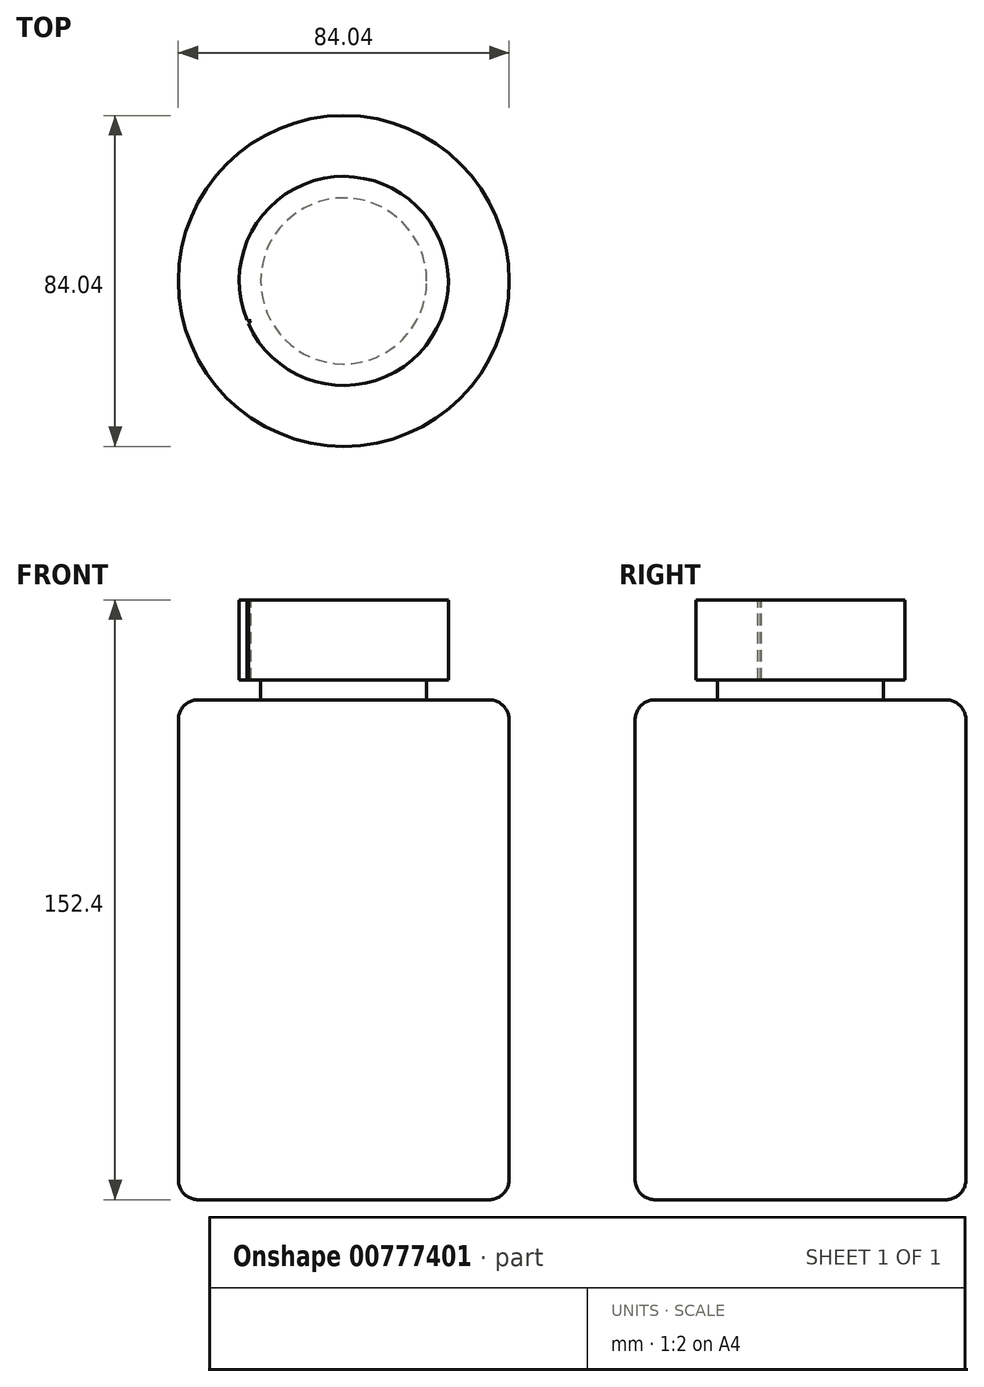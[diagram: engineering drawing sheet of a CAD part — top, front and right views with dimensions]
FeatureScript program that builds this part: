
annotation { "Feature Type Name" : "Feature", "Feature Type Description" : "" }
export const myFeature = defineFeature(function(context is Context, id is Id, definition is map)
    precondition{}
    {
        {
            var Q0;
            Q0=qCreatedBy(makeId("Top.planeOp"),FACE);
            var sketch = newSketch(context, id + "F0", { "sketchPlane" : qUnion([Q0])});
            skCircle(sketch, "E0", {"center": v(0, 0) * mm, "radius": 26.56 * mm});
            skSolve(sketch);
        }
        {
            var Q0;
            Q0 = qSketchRegion(id + "F0", true);
            extrude(context, id + "F1", {"entities" : qUnion([Q0]), "depth" : 20.32 * mm, "offsetDistance" : 25.4 * mm});
        }
        {
            var Q0;
            Q0=qCreatedBy(makeId("Top.planeOp"),FACE);
            var sketch = newSketch(context, id + "F2", { "sketchPlane" : qUnion([Q0])});
            skCircle(sketch, "E1", {"center": v(0, 0) * mm, "radius": 21.09 * mm});
            skSolve(sketch);
        }
        {
            var Q0;
            Q0 = qSketchRegion(id + "F2", true);
            extrude(context, id + "F3", {"entities" : qUnion([Q0]), "operationType" : NewBodyOperationType.ADD, "oppositeDirection" : true, "depth" : 5.08 * mm, "offsetDistance" : 25.4 * mm});
        }
        {
            var Q0;
            Q0=qCreatedBy(makeId("Top.planeOp"),FACE);
            cPlane(context, id + "F4", {"entities" : qUnion([Q0]), "cplaneType" : CPlaneType.OFFSET, "offset" : 5.08 * mm, "oppositeDirection" : true, "width" : 152.4 * mm, "height" : 152.4 * mm});
        }
        {
            var Q0;
            Q0=qCreatedBy(id+"F4.planeOp",FACE);
            var sketch = newSketch(context, id + "F5", { "sketchPlane" : qUnion([Q0])});
            skCircle(sketch, "E2", {"center": v(0, 0) * mm, "radius": 42.02 * mm});
            skSolve(sketch);
        }
        {
            var Q0;
            Q0 = qSketchRegion(id + "F5", true);
            extrude(context, id + "F6", {"entities" : qUnion([Q0]), "operationType" : NewBodyOperationType.ADD, "oppositeDirection" : true, "depth" : 127 * mm, "offsetDistance" : 25.4 * mm});
        }
        {
            var Q0;
            Q0=makeQuery(id+"F6.opExtrude","SWEPT_FACE",FACE,{"disambiguationData":[OSD([sQuery(id+"F5.wireOp",EDGE,"E2")])]});
            fillet(context, id + "F7", {"entities" : qUnion([Q0]), "radius" : 5.08 * mm, "tangentPropagation" : true, "allowEdgeOverflow" : false});
        }
        {
            var Q0;
            Q0=qCreatedBy(makeId("Top.planeOp"),FACE);
            var sketch = newSketch(context, id + "F8", { "sketchPlane" : qUnion([Q0])});
            skCircle(sketch, "E3.cCircle", {"center": v(-67.83, 42.56) * mm, "radius": 11.03 * mm, "construction": true});
            skLineSegment(sketch, "E3.0", {"start": v(-54.4, 44.96) * mm, "end": v(-61.4, 30.54) * mm});
            skLineSegment(sketch, "E3.1", {"start": v(-61.4, 30.54) * mm, "end": v(-77.28, 32.73) * mm});
            skLineSegment(sketch, "E3.2", {"start": v(-77.28, 32.73) * mm, "end": v(-80.1, 48.51) * mm});
            skLineSegment(sketch, "E3.3", {"start": v(-80.1, 48.51) * mm, "end": v(-65.96, 56.07) * mm});
            skLineSegment(sketch, "E3.4", {"start": v(-65.96, 56.07) * mm, "end": v(-54.4, 44.96) * mm});
            skPoint(sketch, "E3.0.midPoint", {"position": v(-57.9, 37.75) * mm});
            skCircle(sketch, "E4.cCircle", {"center": v(-67.83, 42.56) * mm, "radius": 14.44 * mm, "construction": true});
            skLineSegment(sketch, "E4.0", {"start": v(-53.4, 53.05) * mm, "end": v(-53.4, 32.07) * mm});
            skLineSegment(sketch, "E4.1", {"start": v(-53.4, 32.07) * mm, "end": v(-73.34, 25.59) * mm});
            skLineSegment(sketch, "E4.2", {"start": v(-73.34, 25.59) * mm, "end": v(-85.67, 42.56) * mm});
            skLineSegment(sketch, "E4.3", {"start": v(-85.67, 42.56) * mm, "end": v(-73.34, 59.53) * mm});
            skLineSegment(sketch, "E4.4", {"start": v(-73.34, 59.53) * mm, "end": v(-53.4, 53.05) * mm});
            skPoint(sketch, "E4.0.midPoint", {"position": v(-53.4, 42.56) * mm});
            skSolve(sketch);
        }
        {
            var Q0;
            Q0=makeQuery(id+"F8.imprint","IMPRINT",FACE,{"disambiguationData":[TD([[makeQuery(id+"F8.imprint","IMPRINT",EDGE,{"derivedFrom":sQuery(id+"F8.wireOp",EDGE,"E3.0")}),-1.0]])]});
            extrude(context, id + "F9", {"entities" : qUnion([Q0]), "depth" : 25.4 * mm, "offsetDistance" : 25.4 * mm});
        }
        {
            var Q0;
            Q0=qCreatedBy(makeId("Top.planeOp"),FACE);
            var sketch = newSketch(context, id + "F10", { "sketchPlane" : qUnion([Q0])});
            skLineSegment(sketch, "E5", {"start": v(-42.9, 41.98) * mm, "end": v(-26.68, 62.34) * mm});
            skSolve(sketch);
        }
        {
            var Q0;
            Q0=makeQuery(id+"F9.opExtrude","SWEPT_FACE",FACE,{"disambiguationData":[OSD([sQuery(id+"F8.wireOp",EDGE,"E3.3")])]});
            var Q1;
            Q1=sQuery(id+"F10.wireOp",EDGE,"E5");
            sweep(context, id + "F11", {"operationType" : NewBodyOperationType.ADD, "profiles" : qUnion([Q0]), "path" : qUnion([Q1])});
        }
        {
            var Q0;
            Q0=qCreatedBy(makeId("Top.planeOp"),FACE);
            cPlane(context, id + "F12", {"entities" : qUnion([Q0]), "cplaneType" : CPlaneType.OFFSET, "offset" : 20.32 * mm, "width" : 152.4 * mm, "height" : 152.4 * mm});
        }
        {
            var Q0;
            Q0=qCreatedBy(id+"F12.planeOp",FACE);
            var sketch = newSketch(context, id + "F13", { "sketchPlane" : qUnion([Q0])});
            skLineSegment(sketch, "E6", {"start": v(-24.24, -10.84) * mm, "end": v(-23.58, -10.13) * mm});
            skLineSegment(sketch, "E7", {"start": v(-23.58, -10.13) * mm, "end": v(-24.62, -9.96) * mm});
            skArc(sketch, "E8", {"start": v(-24.62, -9.96) * mm, "mid": v(-24.46, -10.41) * mm, "end": v(-24.24, -10.84) * mm});
            skSolve(sketch);
        }
        {
            var Q0;
            Q0=makeQuery(id+"F9.opExtrude","SWEPT_BODY",BODY,{"disambiguationData":[OSD([sQuery(id+"F8.wireOp",EDGE,"E3.0"),sQuery(id+"F8.wireOp",EDGE,"E3.1"),sQuery(id+"F8.wireOp",EDGE,"E3.2"),sQuery(id+"F8.wireOp",EDGE,"E3.3"),sQuery(id+"F8.wireOp",EDGE,"E3.4")])]});
            deleteBodies(context, id + "F14", {"entities" : qUnion([Q0])});
        }
        {
            var Q0;
            Q0=qCreatedBy(makeId("Front.planeOp"),FACE);
            var sketch = newSketch(context, id + "F15", { "sketchPlane" : qUnion([Q0])});
            skLineSegment(sketch, "E9", {"start": v(0, 34.42) * mm, "end": v(0, -30.59) * mm});
            skSolve(sketch);
        }
        {
            var Q0;
            Q0=makeQuery(id+"Fhpd5wwMVkgK8qK_1.97.F13.imprint","IMPRINT",FACE,{"disambiguationData":[TD([[makeQuery(id+"Fhpd5wwMVkgK8qK_1.97.F13.imprint","IMPRINT",EDGE,{"derivedFrom":sQuery(id+"Fhpd5wwMVkgK8qK_1.97.F13.wireOp",EDGE,"E6")}),1.0]])]});
            var Q1;
            Q1=makeQuery(id+"Fhpd5wwMVkgK8qK_1.4.F13.imprint","IMPRINT",FACE,{"disambiguationData":[TD([[makeQuery(id+"Fhpd5wwMVkgK8qK_1.4.F13.imprint","IMPRINT",EDGE,{"derivedFrom":sQuery(id+"Fhpd5wwMVkgK8qK_1.4.F13.wireOp",EDGE,"E6")}),1.0]])]});
            var Q2;
            Q2=makeQuery(id+"Fhpd5wwMVkgK8qK_1.50.F13.imprint","IMPRINT",FACE,{"disambiguationData":[TD([[makeQuery(id+"Fhpd5wwMVkgK8qK_1.50.F13.imprint","IMPRINT",EDGE,{"derivedFrom":sQuery(id+"Fhpd5wwMVkgK8qK_1.50.F13.wireOp",EDGE,"E6")}),1.0]])]});
            var Q3;
            Q3=makeQuery(id+"Fhpd5wwMVkgK8qK_1.19.F13.imprint","IMPRINT",FACE,{"disambiguationData":[TD([[makeQuery(id+"Fhpd5wwMVkgK8qK_1.19.F13.imprint","IMPRINT",EDGE,{"derivedFrom":sQuery(id+"Fhpd5wwMVkgK8qK_1.19.F13.wireOp",EDGE,"E6")}),1.0]])]});
            var Q4;
            Q4=makeQuery(id+"Fhpd5wwMVkgK8qK_1.14.F13.imprint","IMPRINT",FACE,{"disambiguationData":[TD([[makeQuery(id+"Fhpd5wwMVkgK8qK_1.14.F13.imprint","IMPRINT",EDGE,{"derivedFrom":sQuery(id+"Fhpd5wwMVkgK8qK_1.14.F13.wireOp",EDGE,"E6")}),1.0]])]});
            var Q5;
            Q5=makeQuery(id+"Fhpd5wwMVkgK8qK_1.15.F13.imprint","IMPRINT",FACE,{"disambiguationData":[TD([[makeQuery(id+"Fhpd5wwMVkgK8qK_1.15.F13.imprint","IMPRINT",EDGE,{"derivedFrom":sQuery(id+"Fhpd5wwMVkgK8qK_1.15.F13.wireOp",EDGE,"E6")}),1.0]])]});
            var Q6;
            Q6=makeQuery(id+"Fhpd5wwMVkgK8qK_1.90.F13.imprint","IMPRINT",FACE,{"disambiguationData":[TD([[makeQuery(id+"Fhpd5wwMVkgK8qK_1.90.F13.imprint","IMPRINT",EDGE,{"derivedFrom":sQuery(id+"Fhpd5wwMVkgK8qK_1.90.F13.wireOp",EDGE,"E6")}),1.0]])]});
            var Q7;
            Q7=makeQuery(id+"Fhpd5wwMVkgK8qK_1.88.F13.imprint","IMPRINT",FACE,{"disambiguationData":[TD([[makeQuery(id+"Fhpd5wwMVkgK8qK_1.88.F13.imprint","IMPRINT",EDGE,{"derivedFrom":sQuery(id+"Fhpd5wwMVkgK8qK_1.88.F13.wireOp",EDGE,"E6")}),1.0]])]});
            var Q8;
            Q8=makeQuery(id+"Fhpd5wwMVkgK8qK_1.20.F13.imprint","IMPRINT",FACE,{"disambiguationData":[TD([[makeQuery(id+"Fhpd5wwMVkgK8qK_1.20.F13.imprint","IMPRINT",EDGE,{"derivedFrom":sQuery(id+"Fhpd5wwMVkgK8qK_1.20.F13.wireOp",EDGE,"E6")}),1.0]])]});
            var Q9;
            Q9=makeQuery(id+"Fhpd5wwMVkgK8qK_1.18.F13.imprint","IMPRINT",FACE,{"disambiguationData":[TD([[makeQuery(id+"Fhpd5wwMVkgK8qK_1.18.F13.imprint","IMPRINT",EDGE,{"derivedFrom":sQuery(id+"Fhpd5wwMVkgK8qK_1.18.F13.wireOp",EDGE,"E6")}),1.0]])]});
            var Q10;
            Q10=makeQuery(id+"Fhpd5wwMVkgK8qK_1.13.F13.imprint","IMPRINT",FACE,{"disambiguationData":[TD([[makeQuery(id+"Fhpd5wwMVkgK8qK_1.13.F13.imprint","IMPRINT",EDGE,{"derivedFrom":sQuery(id+"Fhpd5wwMVkgK8qK_1.13.F13.wireOp",EDGE,"E6")}),1.0]])]});
            var Q11;
            Q11=makeQuery(id+"Fhpd5wwMVkgK8qK_1.48.F13.imprint","IMPRINT",FACE,{"disambiguationData":[TD([[makeQuery(id+"Fhpd5wwMVkgK8qK_1.48.F13.imprint","IMPRINT",EDGE,{"derivedFrom":sQuery(id+"Fhpd5wwMVkgK8qK_1.48.F13.wireOp",EDGE,"E6")}),1.0]])]});
            var Q12;
            Q12=makeQuery(id+"Fhpd5wwMVkgK8qK_1.5.F13.imprint","IMPRINT",FACE,{"disambiguationData":[TD([[makeQuery(id+"Fhpd5wwMVkgK8qK_1.5.F13.imprint","IMPRINT",EDGE,{"derivedFrom":sQuery(id+"Fhpd5wwMVkgK8qK_1.5.F13.wireOp",EDGE,"E6")}),1.0]])]});
            var Q13;
            Q13=makeQuery(id+"Fhpd5wwMVkgK8qK_1.96.F13.imprint","IMPRINT",FACE,{"disambiguationData":[TD([[makeQuery(id+"Fhpd5wwMVkgK8qK_1.96.F13.imprint","IMPRINT",EDGE,{"derivedFrom":sQuery(id+"Fhpd5wwMVkgK8qK_1.96.F13.wireOp",EDGE,"E6")}),1.0]])]});
            var Q14;
            Q14=makeQuery(id+"Fhpd5wwMVkgK8qK_1.69.F13.imprint","IMPRINT",FACE,{"disambiguationData":[TD([[makeQuery(id+"Fhpd5wwMVkgK8qK_1.69.F13.imprint","IMPRINT",EDGE,{"derivedFrom":sQuery(id+"Fhpd5wwMVkgK8qK_1.69.F13.wireOp",EDGE,"E6")}),1.0]])]});
            var Q15;
            Q15=makeQuery(id+"Fhpd5wwMVkgK8qK_1.45.F13.imprint","IMPRINT",FACE,{"disambiguationData":[TD([[makeQuery(id+"Fhpd5wwMVkgK8qK_1.45.F13.imprint","IMPRINT",EDGE,{"derivedFrom":sQuery(id+"Fhpd5wwMVkgK8qK_1.45.F13.wireOp",EDGE,"E6")}),1.0]])]});
            var Q16;
            Q16=makeQuery(id+"Fhpd5wwMVkgK8qK_1.68.F13.imprint","IMPRINT",FACE,{"disambiguationData":[TD([[makeQuery(id+"Fhpd5wwMVkgK8qK_1.68.F13.imprint","IMPRINT",EDGE,{"derivedFrom":sQuery(id+"Fhpd5wwMVkgK8qK_1.68.F13.wireOp",EDGE,"E6")}),1.0]])]});
            var Q17;
            Q17=makeQuery(id+"Fhpd5wwMVkgK8qK_1.1.F13.imprint","IMPRINT",FACE,{"disambiguationData":[TD([[makeQuery(id+"Fhpd5wwMVkgK8qK_1.1.F13.imprint","IMPRINT",EDGE,{"derivedFrom":sQuery(id+"Fhpd5wwMVkgK8qK_1.1.F13.wireOp",EDGE,"E6")}),1.0]])]});
            var Q18;
            Q18=makeQuery(id+"Fhpd5wwMVkgK8qK_1.8.F13.imprint","IMPRINT",FACE,{"disambiguationData":[TD([[makeQuery(id+"Fhpd5wwMVkgK8qK_1.8.F13.imprint","IMPRINT",EDGE,{"derivedFrom":sQuery(id+"Fhpd5wwMVkgK8qK_1.8.F13.wireOp",EDGE,"E6")}),1.0]])]});
            var Q19;
            Q19=makeQuery(id+"Fhpd5wwMVkgK8qK_1.9.F13.imprint","IMPRINT",FACE,{"disambiguationData":[TD([[makeQuery(id+"Fhpd5wwMVkgK8qK_1.9.F13.imprint","IMPRINT",EDGE,{"derivedFrom":sQuery(id+"Fhpd5wwMVkgK8qK_1.9.F13.wireOp",EDGE,"E6")}),1.0]])]});
            var Q20;
            Q20=makeQuery(id+"Fhpd5wwMVkgK8qK_1.37.F13.imprint","IMPRINT",FACE,{"disambiguationData":[TD([[makeQuery(id+"Fhpd5wwMVkgK8qK_1.37.F13.imprint","IMPRINT",EDGE,{"derivedFrom":sQuery(id+"Fhpd5wwMVkgK8qK_1.37.F13.wireOp",EDGE,"E6")}),1.0]])]});
            var Q21;
            Q21=makeQuery(id+"Fhpd5wwMVkgK8qK_1.21.F13.imprint","IMPRINT",FACE,{"disambiguationData":[TD([[makeQuery(id+"Fhpd5wwMVkgK8qK_1.21.F13.imprint","IMPRINT",EDGE,{"derivedFrom":sQuery(id+"Fhpd5wwMVkgK8qK_1.21.F13.wireOp",EDGE,"E6")}),1.0]])]});
            var Q22;
            Q22=makeQuery(id+"Fhpd5wwMVkgK8qK_1.99.F13.imprint","IMPRINT",FACE,{"disambiguationData":[TD([[makeQuery(id+"Fhpd5wwMVkgK8qK_1.99.F13.imprint","IMPRINT",EDGE,{"derivedFrom":sQuery(id+"Fhpd5wwMVkgK8qK_1.99.F13.wireOp",EDGE,"E6")}),1.0]])]});
            var Q23;
            Q23=makeQuery(id+"Fhpd5wwMVkgK8qK_1.17.F13.imprint","IMPRINT",FACE,{"disambiguationData":[TD([[makeQuery(id+"Fhpd5wwMVkgK8qK_1.17.F13.imprint","IMPRINT",EDGE,{"derivedFrom":sQuery(id+"Fhpd5wwMVkgK8qK_1.17.F13.wireOp",EDGE,"E6")}),1.0]])]});
            var Q24;
            Q24=makeQuery(id+"Fhpd5wwMVkgK8qK_1.38.F13.imprint","IMPRINT",FACE,{"disambiguationData":[TD([[makeQuery(id+"Fhpd5wwMVkgK8qK_1.38.F13.imprint","IMPRINT",EDGE,{"derivedFrom":sQuery(id+"Fhpd5wwMVkgK8qK_1.38.F13.wireOp",EDGE,"E6")}),1.0]])]});
            var Q25;
            Q25=makeQuery(id+"Fhpd5wwMVkgK8qK_1.66.F13.imprint","IMPRINT",FACE,{"disambiguationData":[TD([[makeQuery(id+"Fhpd5wwMVkgK8qK_1.66.F13.imprint","IMPRINT",EDGE,{"derivedFrom":sQuery(id+"Fhpd5wwMVkgK8qK_1.66.F13.wireOp",EDGE,"E6")}),1.0]])]});
            var Q26;
            Q26=makeQuery(id+"Fhpd5wwMVkgK8qK_1.34.F13.imprint","IMPRINT",FACE,{"disambiguationData":[TD([[makeQuery(id+"Fhpd5wwMVkgK8qK_1.34.F13.imprint","IMPRINT",EDGE,{"derivedFrom":sQuery(id+"Fhpd5wwMVkgK8qK_1.34.F13.wireOp",EDGE,"E6")}),1.0]])]});
            var Q27;
            Q27=makeQuery(id+"Fhpd5wwMVkgK8qK_1.52.F13.imprint","IMPRINT",FACE,{"disambiguationData":[TD([[makeQuery(id+"Fhpd5wwMVkgK8qK_1.52.F13.imprint","IMPRINT",EDGE,{"derivedFrom":sQuery(id+"Fhpd5wwMVkgK8qK_1.52.F13.wireOp",EDGE,"E6")}),1.0]])]});
            var Q28;
            Q28=makeQuery(id+"F13.imprint","IMPRINT",FACE,{"disambiguationData":[TD([[makeQuery(id+"F13.imprint","IMPRINT",EDGE,{"derivedFrom":sQuery(id+"F13.wireOp",EDGE,"E6")}),1.0]])]});
            var Q29;
            Q29=makeQuery(id+"Fhpd5wwMVkgK8qK_1.22.F13.imprint","IMPRINT",FACE,{"disambiguationData":[TD([[makeQuery(id+"Fhpd5wwMVkgK8qK_1.22.F13.imprint","IMPRINT",EDGE,{"derivedFrom":sQuery(id+"Fhpd5wwMVkgK8qK_1.22.F13.wireOp",EDGE,"E6")}),1.0]])]});
            var Q30;
            Q30=makeQuery(id+"Fhpd5wwMVkgK8qK_1.44.F13.imprint","IMPRINT",FACE,{"disambiguationData":[TD([[makeQuery(id+"Fhpd5wwMVkgK8qK_1.44.F13.imprint","IMPRINT",EDGE,{"derivedFrom":sQuery(id+"Fhpd5wwMVkgK8qK_1.44.F13.wireOp",EDGE,"E6")}),1.0]])]});
            var Q31;
            Q31=makeQuery(id+"Fhpd5wwMVkgK8qK_1.6.F13.imprint","IMPRINT",FACE,{"disambiguationData":[TD([[makeQuery(id+"Fhpd5wwMVkgK8qK_1.6.F13.imprint","IMPRINT",EDGE,{"derivedFrom":sQuery(id+"Fhpd5wwMVkgK8qK_1.6.F13.wireOp",EDGE,"E6")}),1.0]])]});
            var Q32;
            Q32=makeQuery(id+"Fhpd5wwMVkgK8qK_1.98.F13.imprint","IMPRINT",FACE,{"disambiguationData":[TD([[makeQuery(id+"Fhpd5wwMVkgK8qK_1.98.F13.imprint","IMPRINT",EDGE,{"derivedFrom":sQuery(id+"Fhpd5wwMVkgK8qK_1.98.F13.wireOp",EDGE,"E6")}),1.0]])]});
            var Q33;
            Q33=makeQuery(id+"Fhpd5wwMVkgK8qK_1.11.F13.imprint","IMPRINT",FACE,{"disambiguationData":[TD([[makeQuery(id+"Fhpd5wwMVkgK8qK_1.11.F13.imprint","IMPRINT",EDGE,{"derivedFrom":sQuery(id+"Fhpd5wwMVkgK8qK_1.11.F13.wireOp",EDGE,"E6")}),1.0]])]});
            var Q34;
            Q34=makeQuery(id+"Fhpd5wwMVkgK8qK_1.10.F13.imprint","IMPRINT",FACE,{"disambiguationData":[TD([[makeQuery(id+"Fhpd5wwMVkgK8qK_1.10.F13.imprint","IMPRINT",EDGE,{"derivedFrom":sQuery(id+"Fhpd5wwMVkgK8qK_1.10.F13.wireOp",EDGE,"E6")}),1.0]])]});
            var Q35;
            Q35=makeQuery(id+"Fhpd5wwMVkgK8qK_1.7.F13.imprint","IMPRINT",FACE,{"disambiguationData":[TD([[makeQuery(id+"Fhpd5wwMVkgK8qK_1.7.F13.imprint","IMPRINT",EDGE,{"derivedFrom":sQuery(id+"Fhpd5wwMVkgK8qK_1.7.F13.wireOp",EDGE,"E6")}),1.0]])]});
            var Q36;
            Q36=makeQuery(id+"Fhpd5wwMVkgK8qK_1.75.F13.imprint","IMPRINT",FACE,{"disambiguationData":[TD([[makeQuery(id+"Fhpd5wwMVkgK8qK_1.75.F13.imprint","IMPRINT",EDGE,{"derivedFrom":sQuery(id+"Fhpd5wwMVkgK8qK_1.75.F13.wireOp",EDGE,"E6")}),1.0]])]});
            var Q37;
            Q37=makeQuery(id+"Fhpd5wwMVkgK8qK_1.65.F13.imprint","IMPRINT",FACE,{"disambiguationData":[TD([[makeQuery(id+"Fhpd5wwMVkgK8qK_1.65.F13.imprint","IMPRINT",EDGE,{"derivedFrom":sQuery(id+"Fhpd5wwMVkgK8qK_1.65.F13.wireOp",EDGE,"E6")}),1.0]])]});
            var Q38;
            Q38=makeQuery(id+"Fhpd5wwMVkgK8qK_1.89.F13.imprint","IMPRINT",FACE,{"disambiguationData":[TD([[makeQuery(id+"Fhpd5wwMVkgK8qK_1.89.F13.imprint","IMPRINT",EDGE,{"derivedFrom":sQuery(id+"Fhpd5wwMVkgK8qK_1.89.F13.wireOp",EDGE,"E6")}),1.0]])]});
            var Q39;
            Q39=makeQuery(id+"Fhpd5wwMVkgK8qK_1.91.F13.imprint","IMPRINT",FACE,{"disambiguationData":[TD([[makeQuery(id+"Fhpd5wwMVkgK8qK_1.91.F13.imprint","IMPRINT",EDGE,{"derivedFrom":sQuery(id+"Fhpd5wwMVkgK8qK_1.91.F13.wireOp",EDGE,"E6")}),1.0]])]});
            var Q40;
            Q40=makeQuery(id+"Fhpd5wwMVkgK8qK_1.71.F13.imprint","IMPRINT",FACE,{"disambiguationData":[TD([[makeQuery(id+"Fhpd5wwMVkgK8qK_1.71.F13.imprint","IMPRINT",EDGE,{"derivedFrom":sQuery(id+"Fhpd5wwMVkgK8qK_1.71.F13.wireOp",EDGE,"E6")}),1.0]])]});
            var Q41;
            Q41=makeQuery(id+"Fhpd5wwMVkgK8qK_1.16.F13.imprint","IMPRINT",FACE,{"disambiguationData":[TD([[makeQuery(id+"Fhpd5wwMVkgK8qK_1.16.F13.imprint","IMPRINT",EDGE,{"derivedFrom":sQuery(id+"Fhpd5wwMVkgK8qK_1.16.F13.wireOp",EDGE,"E6")}),1.0]])]});
            var Q42;
            Q42=makeQuery(id+"Fhpd5wwMVkgK8qK_1.92.F13.imprint","IMPRINT",FACE,{"disambiguationData":[TD([[makeQuery(id+"Fhpd5wwMVkgK8qK_1.92.F13.imprint","IMPRINT",EDGE,{"derivedFrom":sQuery(id+"Fhpd5wwMVkgK8qK_1.92.F13.wireOp",EDGE,"E6")}),1.0]])]});
            var Q43;
            Q43=makeQuery(id+"Fhpd5wwMVkgK8qK_1.49.F13.imprint","IMPRINT",FACE,{"disambiguationData":[TD([[makeQuery(id+"Fhpd5wwMVkgK8qK_1.49.F13.imprint","IMPRINT",EDGE,{"derivedFrom":sQuery(id+"Fhpd5wwMVkgK8qK_1.49.F13.wireOp",EDGE,"E6")}),1.0]])]});
            var Q44;
            Q44=makeQuery(id+"Fhpd5wwMVkgK8qK_1.46.F13.imprint","IMPRINT",FACE,{"disambiguationData":[TD([[makeQuery(id+"Fhpd5wwMVkgK8qK_1.46.F13.imprint","IMPRINT",EDGE,{"derivedFrom":sQuery(id+"Fhpd5wwMVkgK8qK_1.46.F13.wireOp",EDGE,"E6")}),1.0]])]});
            var Q45;
            Q45=makeQuery(id+"Fhpd5wwMVkgK8qK_1.2.F13.imprint","IMPRINT",FACE,{"disambiguationData":[TD([[makeQuery(id+"Fhpd5wwMVkgK8qK_1.2.F13.imprint","IMPRINT",EDGE,{"derivedFrom":sQuery(id+"Fhpd5wwMVkgK8qK_1.2.F13.wireOp",EDGE,"E6")}),1.0]])]});
            var Q46;
            Q46=makeQuery(id+"Fhpd5wwMVkgK8qK_1.3.F13.imprint","IMPRINT",FACE,{"disambiguationData":[TD([[makeQuery(id+"Fhpd5wwMVkgK8qK_1.3.F13.imprint","IMPRINT",EDGE,{"derivedFrom":sQuery(id+"Fhpd5wwMVkgK8qK_1.3.F13.wireOp",EDGE,"E6")}),1.0]])]});
            var Q47;
            Q47=makeQuery(id+"Fhpd5wwMVkgK8qK_1.93.F13.imprint","IMPRINT",FACE,{"disambiguationData":[TD([[makeQuery(id+"Fhpd5wwMVkgK8qK_1.93.F13.imprint","IMPRINT",EDGE,{"derivedFrom":sQuery(id+"Fhpd5wwMVkgK8qK_1.93.F13.wireOp",EDGE,"E6")}),1.0]])]});
            var Q48;
            Q48=makeQuery(id+"Fhpd5wwMVkgK8qK_1.23.F13.imprint","IMPRINT",FACE,{"disambiguationData":[TD([[makeQuery(id+"Fhpd5wwMVkgK8qK_1.23.F13.imprint","IMPRINT",EDGE,{"derivedFrom":sQuery(id+"Fhpd5wwMVkgK8qK_1.23.F13.wireOp",EDGE,"E6")}),1.0]])]});
            var Q49;
            Q49=makeQuery(id+"Fhpd5wwMVkgK8qK_1.87.F13.imprint","IMPRINT",FACE,{"disambiguationData":[TD([[makeQuery(id+"Fhpd5wwMVkgK8qK_1.87.F13.imprint","IMPRINT",EDGE,{"derivedFrom":sQuery(id+"Fhpd5wwMVkgK8qK_1.87.F13.wireOp",EDGE,"E6")}),1.0]])]});
            var Q50;
            Q50=makeQuery(id+"Fhpd5wwMVkgK8qK_1.67.F13.imprint","IMPRINT",FACE,{"disambiguationData":[TD([[makeQuery(id+"Fhpd5wwMVkgK8qK_1.67.F13.imprint","IMPRINT",EDGE,{"derivedFrom":sQuery(id+"Fhpd5wwMVkgK8qK_1.67.F13.wireOp",EDGE,"E6")}),1.0]])]});
            var Q51;
            Q51=makeQuery(id+"Fhpd5wwMVkgK8qK_1.47.F13.imprint","IMPRINT",FACE,{"disambiguationData":[TD([[makeQuery(id+"Fhpd5wwMVkgK8qK_1.47.F13.imprint","IMPRINT",EDGE,{"derivedFrom":sQuery(id+"Fhpd5wwMVkgK8qK_1.47.F13.wireOp",EDGE,"E6")}),1.0]])]});
            var Q52;
            Q52=makeQuery(id+"Fhpd5wwMVkgK8qK_1.85.F13.imprint","IMPRINT",FACE,{"disambiguationData":[TD([[makeQuery(id+"Fhpd5wwMVkgK8qK_1.85.F13.imprint","IMPRINT",EDGE,{"derivedFrom":sQuery(id+"Fhpd5wwMVkgK8qK_1.85.F13.wireOp",EDGE,"E6")}),1.0]])]});
            var Q53;
            Q53=makeQuery(id+"Fhpd5wwMVkgK8qK_1.53.F13.imprint","IMPRINT",FACE,{"disambiguationData":[TD([[makeQuery(id+"Fhpd5wwMVkgK8qK_1.53.F13.imprint","IMPRINT",EDGE,{"derivedFrom":sQuery(id+"Fhpd5wwMVkgK8qK_1.53.F13.wireOp",EDGE,"E6")}),1.0]])]});
            var Q54;
            Q54=makeQuery(id+"Fhpd5wwMVkgK8qK_1.33.F13.imprint","IMPRINT",FACE,{"disambiguationData":[TD([[makeQuery(id+"Fhpd5wwMVkgK8qK_1.33.F13.imprint","IMPRINT",EDGE,{"derivedFrom":sQuery(id+"Fhpd5wwMVkgK8qK_1.33.F13.wireOp",EDGE,"E6")}),1.0]])]});
            var Q55;
            Q55=makeQuery(id+"Fhpd5wwMVkgK8qK_1.95.F13.imprint","IMPRINT",FACE,{"disambiguationData":[TD([[makeQuery(id+"Fhpd5wwMVkgK8qK_1.95.F13.imprint","IMPRINT",EDGE,{"derivedFrom":sQuery(id+"Fhpd5wwMVkgK8qK_1.95.F13.wireOp",EDGE,"E6")}),1.0]])]});
            var Q56;
            Q56=makeQuery(id+"Fhpd5wwMVkgK8qK_1.12.F13.imprint","IMPRINT",FACE,{"disambiguationData":[TD([[makeQuery(id+"Fhpd5wwMVkgK8qK_1.12.F13.imprint","IMPRINT",EDGE,{"derivedFrom":sQuery(id+"Fhpd5wwMVkgK8qK_1.12.F13.wireOp",EDGE,"E6")}),1.0]])]});
            var Q57;
            Q57=makeQuery(id+"Fhpd5wwMVkgK8qK_1.94.F13.imprint","IMPRINT",FACE,{"disambiguationData":[TD([[makeQuery(id+"Fhpd5wwMVkgK8qK_1.94.F13.imprint","IMPRINT",EDGE,{"derivedFrom":sQuery(id+"Fhpd5wwMVkgK8qK_1.94.F13.wireOp",EDGE,"E6")}),1.0]])]});
            var Q58;
            Q58=makeQuery(id+"Fhpd5wwMVkgK8qK_1.58.F13.imprint","IMPRINT",FACE,{"disambiguationData":[TD([[makeQuery(id+"Fhpd5wwMVkgK8qK_1.58.F13.imprint","IMPRINT",EDGE,{"derivedFrom":sQuery(id+"Fhpd5wwMVkgK8qK_1.58.F13.wireOp",EDGE,"E6")}),1.0]])]});
            var Q59;
            Q59=makeQuery(id+"Fhpd5wwMVkgK8qK_1.54.F13.imprint","IMPRINT",FACE,{"disambiguationData":[TD([[makeQuery(id+"Fhpd5wwMVkgK8qK_1.54.F13.imprint","IMPRINT",EDGE,{"derivedFrom":sQuery(id+"Fhpd5wwMVkgK8qK_1.54.F13.wireOp",EDGE,"E6")}),1.0]])]});
            var Q60;
            Q60=makeQuery(id+"Fhpd5wwMVkgK8qK_1.86.F13.imprint","IMPRINT",FACE,{"disambiguationData":[TD([[makeQuery(id+"Fhpd5wwMVkgK8qK_1.86.F13.imprint","IMPRINT",EDGE,{"derivedFrom":sQuery(id+"Fhpd5wwMVkgK8qK_1.86.F13.wireOp",EDGE,"E6")}),1.0]])]});
            var Q61;
            Q61=makeQuery(id+"Fhpd5wwMVkgK8qK_1.43.F13.imprint","IMPRINT",FACE,{"disambiguationData":[TD([[makeQuery(id+"Fhpd5wwMVkgK8qK_1.43.F13.imprint","IMPRINT",EDGE,{"derivedFrom":sQuery(id+"Fhpd5wwMVkgK8qK_1.43.F13.wireOp",EDGE,"E6")}),1.0]])]});
            var Q62;
            Q62=makeQuery(id+"Fhpd5wwMVkgK8qK_1.59.F13.imprint","IMPRINT",FACE,{"disambiguationData":[TD([[makeQuery(id+"Fhpd5wwMVkgK8qK_1.59.F13.imprint","IMPRINT",EDGE,{"derivedFrom":sQuery(id+"Fhpd5wwMVkgK8qK_1.59.F13.wireOp",EDGE,"E6")}),1.0]])]});
            var Q63;
            Q63=makeQuery(id+"Fhpd5wwMVkgK8qK_1.25.F13.imprint","IMPRINT",FACE,{"disambiguationData":[TD([[makeQuery(id+"Fhpd5wwMVkgK8qK_1.25.F13.imprint","IMPRINT",EDGE,{"derivedFrom":sQuery(id+"Fhpd5wwMVkgK8qK_1.25.F13.wireOp",EDGE,"E6")}),1.0]])]});
            var Q64;
            Q64=makeQuery(id+"Fhpd5wwMVkgK8qK_1.61.F13.imprint","IMPRINT",FACE,{"disambiguationData":[TD([[makeQuery(id+"Fhpd5wwMVkgK8qK_1.61.F13.imprint","IMPRINT",EDGE,{"derivedFrom":sQuery(id+"Fhpd5wwMVkgK8qK_1.61.F13.wireOp",EDGE,"E6")}),1.0]])]});
            var Q65;
            Q65=makeQuery(id+"Fhpd5wwMVkgK8qK_1.57.F13.imprint","IMPRINT",FACE,{"disambiguationData":[TD([[makeQuery(id+"Fhpd5wwMVkgK8qK_1.57.F13.imprint","IMPRINT",EDGE,{"derivedFrom":sQuery(id+"Fhpd5wwMVkgK8qK_1.57.F13.wireOp",EDGE,"E6")}),1.0]])]});
            var Q66;
            Q66=makeQuery(id+"Fhpd5wwMVkgK8qK_1.39.F13.imprint","IMPRINT",FACE,{"disambiguationData":[TD([[makeQuery(id+"Fhpd5wwMVkgK8qK_1.39.F13.imprint","IMPRINT",EDGE,{"derivedFrom":sQuery(id+"Fhpd5wwMVkgK8qK_1.39.F13.wireOp",EDGE,"E6")}),1.0]])]});
            var Q67;
            Q67=makeQuery(id+"Fhpd5wwMVkgK8qK_1.51.F13.imprint","IMPRINT",FACE,{"disambiguationData":[TD([[makeQuery(id+"Fhpd5wwMVkgK8qK_1.51.F13.imprint","IMPRINT",EDGE,{"derivedFrom":sQuery(id+"Fhpd5wwMVkgK8qK_1.51.F13.wireOp",EDGE,"E6")}),1.0]])]});
            var Q68;
            Q68=makeQuery(id+"Fhpd5wwMVkgK8qK_1.77.F13.imprint","IMPRINT",FACE,{"disambiguationData":[TD([[makeQuery(id+"Fhpd5wwMVkgK8qK_1.77.F13.imprint","IMPRINT",EDGE,{"derivedFrom":sQuery(id+"Fhpd5wwMVkgK8qK_1.77.F13.wireOp",EDGE,"E6")}),1.0]])]});
            var Q69;
            Q69=makeQuery(id+"Fhpd5wwMVkgK8qK_1.30.F13.imprint","IMPRINT",FACE,{"disambiguationData":[TD([[makeQuery(id+"Fhpd5wwMVkgK8qK_1.30.F13.imprint","IMPRINT",EDGE,{"derivedFrom":sQuery(id+"Fhpd5wwMVkgK8qK_1.30.F13.wireOp",EDGE,"E6")}),1.0]])]});
            var Q70;
            Q70=makeQuery(id+"Fhpd5wwMVkgK8qK_1.72.F13.imprint","IMPRINT",FACE,{"disambiguationData":[TD([[makeQuery(id+"Fhpd5wwMVkgK8qK_1.72.F13.imprint","IMPRINT",EDGE,{"derivedFrom":sQuery(id+"Fhpd5wwMVkgK8qK_1.72.F13.wireOp",EDGE,"E6")}),1.0]])]});
            var Q71;
            Q71=makeQuery(id+"Fhpd5wwMVkgK8qK_1.56.F13.imprint","IMPRINT",FACE,{"disambiguationData":[TD([[makeQuery(id+"Fhpd5wwMVkgK8qK_1.56.F13.imprint","IMPRINT",EDGE,{"derivedFrom":sQuery(id+"Fhpd5wwMVkgK8qK_1.56.F13.wireOp",EDGE,"E6")}),1.0]])]});
            var Q72;
            Q72=makeQuery(id+"Fhpd5wwMVkgK8qK_1.36.F13.imprint","IMPRINT",FACE,{"disambiguationData":[TD([[makeQuery(id+"Fhpd5wwMVkgK8qK_1.36.F13.imprint","IMPRINT",EDGE,{"derivedFrom":sQuery(id+"Fhpd5wwMVkgK8qK_1.36.F13.wireOp",EDGE,"E6")}),1.0]])]});
            var Q73;
            Q73=makeQuery(id+"Fhpd5wwMVkgK8qK_1.84.F13.imprint","IMPRINT",FACE,{"disambiguationData":[TD([[makeQuery(id+"Fhpd5wwMVkgK8qK_1.84.F13.imprint","IMPRINT",EDGE,{"derivedFrom":sQuery(id+"Fhpd5wwMVkgK8qK_1.84.F13.wireOp",EDGE,"E6")}),1.0]])]});
            var Q74;
            Q74=makeQuery(id+"Fhpd5wwMVkgK8qK_1.78.F13.imprint","IMPRINT",FACE,{"disambiguationData":[TD([[makeQuery(id+"Fhpd5wwMVkgK8qK_1.78.F13.imprint","IMPRINT",EDGE,{"derivedFrom":sQuery(id+"Fhpd5wwMVkgK8qK_1.78.F13.wireOp",EDGE,"E6")}),1.0]])]});
            var Q75;
            Q75=makeQuery(id+"Fhpd5wwMVkgK8qK_1.29.F13.imprint","IMPRINT",FACE,{"disambiguationData":[TD([[makeQuery(id+"Fhpd5wwMVkgK8qK_1.29.F13.imprint","IMPRINT",EDGE,{"derivedFrom":sQuery(id+"Fhpd5wwMVkgK8qK_1.29.F13.wireOp",EDGE,"E6")}),1.0]])]});
            var Q76;
            Q76=makeQuery(id+"Fhpd5wwMVkgK8qK_1.41.F13.imprint","IMPRINT",FACE,{"disambiguationData":[TD([[makeQuery(id+"Fhpd5wwMVkgK8qK_1.41.F13.imprint","IMPRINT",EDGE,{"derivedFrom":sQuery(id+"Fhpd5wwMVkgK8qK_1.41.F13.wireOp",EDGE,"E6")}),1.0]])]});
            var Q77;
            Q77=makeQuery(id+"Fhpd5wwMVkgK8qK_1.73.F13.imprint","IMPRINT",FACE,{"disambiguationData":[TD([[makeQuery(id+"Fhpd5wwMVkgK8qK_1.73.F13.imprint","IMPRINT",EDGE,{"derivedFrom":sQuery(id+"Fhpd5wwMVkgK8qK_1.73.F13.wireOp",EDGE,"E6")}),1.0]])]});
            var Q78;
            Q78=makeQuery(id+"Fhpd5wwMVkgK8qK_1.27.F13.imprint","IMPRINT",FACE,{"disambiguationData":[TD([[makeQuery(id+"Fhpd5wwMVkgK8qK_1.27.F13.imprint","IMPRINT",EDGE,{"derivedFrom":sQuery(id+"Fhpd5wwMVkgK8qK_1.27.F13.wireOp",EDGE,"E6")}),1.0]])]});
            var Q79;
            Q79=makeQuery(id+"Fhpd5wwMVkgK8qK_1.35.F13.imprint","IMPRINT",FACE,{"disambiguationData":[TD([[makeQuery(id+"Fhpd5wwMVkgK8qK_1.35.F13.imprint","IMPRINT",EDGE,{"derivedFrom":sQuery(id+"Fhpd5wwMVkgK8qK_1.35.F13.wireOp",EDGE,"E6")}),1.0]])]});
            var Q80;
            Q80=makeQuery(id+"Fhpd5wwMVkgK8qK_1.42.F13.imprint","IMPRINT",FACE,{"disambiguationData":[TD([[makeQuery(id+"Fhpd5wwMVkgK8qK_1.42.F13.imprint","IMPRINT",EDGE,{"derivedFrom":sQuery(id+"Fhpd5wwMVkgK8qK_1.42.F13.wireOp",EDGE,"E6")}),1.0]])]});
            var Q81;
            Q81=makeQuery(id+"Fhpd5wwMVkgK8qK_1.74.F13.imprint","IMPRINT",FACE,{"disambiguationData":[TD([[makeQuery(id+"Fhpd5wwMVkgK8qK_1.74.F13.imprint","IMPRINT",EDGE,{"derivedFrom":sQuery(id+"Fhpd5wwMVkgK8qK_1.74.F13.wireOp",EDGE,"E6")}),1.0]])]});
            var Q82;
            Q82=makeQuery(id+"Fhpd5wwMVkgK8qK_1.60.F13.imprint","IMPRINT",FACE,{"disambiguationData":[TD([[makeQuery(id+"Fhpd5wwMVkgK8qK_1.60.F13.imprint","IMPRINT",EDGE,{"derivedFrom":sQuery(id+"Fhpd5wwMVkgK8qK_1.60.F13.wireOp",EDGE,"E6")}),1.0]])]});
            var Q83;
            Q83=makeQuery(id+"Fhpd5wwMVkgK8qK_1.28.F13.imprint","IMPRINT",FACE,{"disambiguationData":[TD([[makeQuery(id+"Fhpd5wwMVkgK8qK_1.28.F13.imprint","IMPRINT",EDGE,{"derivedFrom":sQuery(id+"Fhpd5wwMVkgK8qK_1.28.F13.wireOp",EDGE,"E6")}),1.0]])]});
            var Q84;
            Q84=makeQuery(id+"Fhpd5wwMVkgK8qK_1.26.F13.imprint","IMPRINT",FACE,{"disambiguationData":[TD([[makeQuery(id+"Fhpd5wwMVkgK8qK_1.26.F13.imprint","IMPRINT",EDGE,{"derivedFrom":sQuery(id+"Fhpd5wwMVkgK8qK_1.26.F13.wireOp",EDGE,"E6")}),1.0]])]});
            var Q85;
            Q85=makeQuery(id+"Fhpd5wwMVkgK8qK_1.70.F13.imprint","IMPRINT",FACE,{"disambiguationData":[TD([[makeQuery(id+"Fhpd5wwMVkgK8qK_1.70.F13.imprint","IMPRINT",EDGE,{"derivedFrom":sQuery(id+"Fhpd5wwMVkgK8qK_1.70.F13.wireOp",EDGE,"E6")}),1.0]])]});
            var Q86;
            Q86=makeQuery(id+"Fhpd5wwMVkgK8qK_1.24.F13.imprint","IMPRINT",FACE,{"disambiguationData":[TD([[makeQuery(id+"Fhpd5wwMVkgK8qK_1.24.F13.imprint","IMPRINT",EDGE,{"derivedFrom":sQuery(id+"Fhpd5wwMVkgK8qK_1.24.F13.wireOp",EDGE,"E6")}),1.0]])]});
            var Q87;
            Q87=makeQuery(id+"Fhpd5wwMVkgK8qK_1.80.F13.imprint","IMPRINT",FACE,{"disambiguationData":[TD([[makeQuery(id+"Fhpd5wwMVkgK8qK_1.80.F13.imprint","IMPRINT",EDGE,{"derivedFrom":sQuery(id+"Fhpd5wwMVkgK8qK_1.80.F13.wireOp",EDGE,"E6")}),1.0]])]});
            var Q88;
            Q88=makeQuery(id+"Fhpd5wwMVkgK8qK_1.76.F13.imprint","IMPRINT",FACE,{"disambiguationData":[TD([[makeQuery(id+"Fhpd5wwMVkgK8qK_1.76.F13.imprint","IMPRINT",EDGE,{"derivedFrom":sQuery(id+"Fhpd5wwMVkgK8qK_1.76.F13.wireOp",EDGE,"E6")}),1.0]])]});
            var Q89;
            Q89=makeQuery(id+"Fhpd5wwMVkgK8qK_1.79.F13.imprint","IMPRINT",FACE,{"disambiguationData":[TD([[makeQuery(id+"Fhpd5wwMVkgK8qK_1.79.F13.imprint","IMPRINT",EDGE,{"derivedFrom":sQuery(id+"Fhpd5wwMVkgK8qK_1.79.F13.wireOp",EDGE,"E6")}),1.0]])]});
            var Q90;
            Q90=makeQuery(id+"Fhpd5wwMVkgK8qK_1.63.F13.imprint","IMPRINT",FACE,{"disambiguationData":[TD([[makeQuery(id+"Fhpd5wwMVkgK8qK_1.63.F13.imprint","IMPRINT",EDGE,{"derivedFrom":sQuery(id+"Fhpd5wwMVkgK8qK_1.63.F13.wireOp",EDGE,"E6")}),1.0]])]});
            var Q91;
            Q91=makeQuery(id+"Fhpd5wwMVkgK8qK_1.40.F13.imprint","IMPRINT",FACE,{"disambiguationData":[TD([[makeQuery(id+"Fhpd5wwMVkgK8qK_1.40.F13.imprint","IMPRINT",EDGE,{"derivedFrom":sQuery(id+"Fhpd5wwMVkgK8qK_1.40.F13.wireOp",EDGE,"E6")}),1.0]])]});
            var Q92;
            Q92=makeQuery(id+"Fhpd5wwMVkgK8qK_1.64.F13.imprint","IMPRINT",FACE,{"disambiguationData":[TD([[makeQuery(id+"Fhpd5wwMVkgK8qK_1.64.F13.imprint","IMPRINT",EDGE,{"derivedFrom":sQuery(id+"Fhpd5wwMVkgK8qK_1.64.F13.wireOp",EDGE,"E6")}),1.0]])]});
            var Q93;
            Q93=makeQuery(id+"Fhpd5wwMVkgK8qK_1.32.F13.imprint","IMPRINT",FACE,{"disambiguationData":[TD([[makeQuery(id+"Fhpd5wwMVkgK8qK_1.32.F13.imprint","IMPRINT",EDGE,{"derivedFrom":sQuery(id+"Fhpd5wwMVkgK8qK_1.32.F13.wireOp",EDGE,"E6")}),1.0]])]});
            var Q94;
            Q94=makeQuery(id+"Fhpd5wwMVkgK8qK_1.31.F13.imprint","IMPRINT",FACE,{"disambiguationData":[TD([[makeQuery(id+"Fhpd5wwMVkgK8qK_1.31.F13.imprint","IMPRINT",EDGE,{"derivedFrom":sQuery(id+"Fhpd5wwMVkgK8qK_1.31.F13.wireOp",EDGE,"E6")}),1.0]])]});
            var Q95;
            Q95=makeQuery(id+"Fhpd5wwMVkgK8qK_1.62.F13.imprint","IMPRINT",FACE,{"disambiguationData":[TD([[makeQuery(id+"Fhpd5wwMVkgK8qK_1.62.F13.imprint","IMPRINT",EDGE,{"derivedFrom":sQuery(id+"Fhpd5wwMVkgK8qK_1.62.F13.wireOp",EDGE,"E6")}),1.0]])]});
            var Q96;
            Q96=makeQuery(id+"Fhpd5wwMVkgK8qK_1.82.F13.imprint","IMPRINT",FACE,{"disambiguationData":[TD([[makeQuery(id+"Fhpd5wwMVkgK8qK_1.82.F13.imprint","IMPRINT",EDGE,{"derivedFrom":sQuery(id+"Fhpd5wwMVkgK8qK_1.82.F13.wireOp",EDGE,"E6")}),1.0]])]});
            var Q97;
            Q97=makeQuery(id+"Fhpd5wwMVkgK8qK_1.83.F13.imprint","IMPRINT",FACE,{"disambiguationData":[TD([[makeQuery(id+"Fhpd5wwMVkgK8qK_1.83.F13.imprint","IMPRINT",EDGE,{"derivedFrom":sQuery(id+"Fhpd5wwMVkgK8qK_1.83.F13.wireOp",EDGE,"E6")}),1.0]])]});
            var Q98;
            Q98=makeQuery(id+"Fhpd5wwMVkgK8qK_1.81.F13.imprint","IMPRINT",FACE,{"disambiguationData":[TD([[makeQuery(id+"Fhpd5wwMVkgK8qK_1.81.F13.imprint","IMPRINT",EDGE,{"derivedFrom":sQuery(id+"Fhpd5wwMVkgK8qK_1.81.F13.wireOp",EDGE,"E6")}),1.0]])]});
            var Q99;
            Q99=makeQuery(id+"Fhpd5wwMVkgK8qK_1.55.F13.imprint","IMPRINT",FACE,{"disambiguationData":[TD([[makeQuery(id+"Fhpd5wwMVkgK8qK_1.55.F13.imprint","IMPRINT",EDGE,{"derivedFrom":sQuery(id+"Fhpd5wwMVkgK8qK_1.55.F13.wireOp",EDGE,"E6")}),1.0]])]});
            var Q100;
            Q100=makeQuery(id+"Fhpd5wwMVkgK8qK_1.100.F13.imprint","IMPRINT",FACE,{"disambiguationData":[TD([[makeQuery(id+"Fhpd5wwMVkgK8qK_1.100.F13.imprint","IMPRINT",EDGE,{"derivedFrom":sQuery(id+"Fhpd5wwMVkgK8qK_1.100.F13.wireOp",EDGE,"E6")}),1.0]])]});
            var Q101;
            Q101=makeQuery(id+"Fhpd5wwMVkgK8qK_1.101.F13.imprint","IMPRINT",FACE,{"disambiguationData":[TD([[makeQuery(id+"Fhpd5wwMVkgK8qK_1.101.F13.imprint","IMPRINT",EDGE,{"derivedFrom":sQuery(id+"Fhpd5wwMVkgK8qK_1.101.F13.wireOp",EDGE,"E6")}),1.0]])]});
            var Q102;
            Q102=makeQuery(id+"Fhpd5wwMVkgK8qK_1.102.F13.imprint","IMPRINT",FACE,{"disambiguationData":[TD([[makeQuery(id+"Fhpd5wwMVkgK8qK_1.102.F13.imprint","IMPRINT",EDGE,{"derivedFrom":sQuery(id+"Fhpd5wwMVkgK8qK_1.102.F13.wireOp",EDGE,"E6")}),1.0]])]});
            var Q103;
            Q103=makeQuery(id+"Fhpd5wwMVkgK8qK_1.104.F13.imprint","IMPRINT",FACE,{"disambiguationData":[TD([[makeQuery(id+"Fhpd5wwMVkgK8qK_1.104.F13.imprint","IMPRINT",EDGE,{"derivedFrom":sQuery(id+"Fhpd5wwMVkgK8qK_1.104.F13.wireOp",EDGE,"E6")}),1.0]])]});
            var Q104;
            Q104=makeQuery(id+"Fhpd5wwMVkgK8qK_1.103.F13.imprint","IMPRINT",FACE,{"disambiguationData":[TD([[makeQuery(id+"Fhpd5wwMVkgK8qK_1.103.F13.imprint","IMPRINT",EDGE,{"derivedFrom":sQuery(id+"Fhpd5wwMVkgK8qK_1.103.F13.wireOp",EDGE,"E6")}),1.0]])]});
            var Q105;
            Q105=makeQuery(id+"Fhpd5wwMVkgK8qK_1.105.F13.imprint","IMPRINT",FACE,{"disambiguationData":[TD([[makeQuery(id+"Fhpd5wwMVkgK8qK_1.105.F13.imprint","IMPRINT",EDGE,{"derivedFrom":sQuery(id+"Fhpd5wwMVkgK8qK_1.105.F13.wireOp",EDGE,"E6")}),1.0]])]});
            var Q106;
            Q106=makeQuery(id+"Fhpd5wwMVkgK8qK_1.106.F13.imprint","IMPRINT",FACE,{"disambiguationData":[TD([[makeQuery(id+"Fhpd5wwMVkgK8qK_1.106.F13.imprint","IMPRINT",EDGE,{"derivedFrom":sQuery(id+"Fhpd5wwMVkgK8qK_1.106.F13.wireOp",EDGE,"E6")}),1.0]])]});
            var Q107;
            Q107=makeQuery(id+"Fhpd5wwMVkgK8qK_1.107.F13.imprint","IMPRINT",FACE,{"disambiguationData":[TD([[makeQuery(id+"Fhpd5wwMVkgK8qK_1.107.F13.imprint","IMPRINT",EDGE,{"derivedFrom":sQuery(id+"Fhpd5wwMVkgK8qK_1.107.F13.wireOp",EDGE,"E6")}),1.0]])]});
            var Q108;
            Q108=makeQuery(id+"Fhpd5wwMVkgK8qK_1.108.F13.imprint","IMPRINT",FACE,{"disambiguationData":[TD([[makeQuery(id+"Fhpd5wwMVkgK8qK_1.108.F13.imprint","IMPRINT",EDGE,{"derivedFrom":sQuery(id+"Fhpd5wwMVkgK8qK_1.108.F13.wireOp",EDGE,"E6")}),1.0]])]});
            var Q109;
            Q109=makeQuery(id+"Fhpd5wwMVkgK8qK_1.109.F13.imprint","IMPRINT",FACE,{"disambiguationData":[TD([[makeQuery(id+"Fhpd5wwMVkgK8qK_1.109.F13.imprint","IMPRINT",EDGE,{"derivedFrom":sQuery(id+"Fhpd5wwMVkgK8qK_1.109.F13.wireOp",EDGE,"E6")}),1.0]])]});
            var Q110;
            Q110=makeQuery(id+"Fhpd5wwMVkgK8qK_1.147.F13.imprint","IMPRINT",FACE,{"disambiguationData":[TD([[makeQuery(id+"Fhpd5wwMVkgK8qK_1.147.F13.imprint","IMPRINT",EDGE,{"derivedFrom":sQuery(id+"Fhpd5wwMVkgK8qK_1.147.F13.wireOp",EDGE,"E6")}),1.0]])]});
            var Q111;
            Q111=makeQuery(id+"Fhpd5wwMVkgK8qK_1.117.F13.imprint","IMPRINT",FACE,{"disambiguationData":[TD([[makeQuery(id+"Fhpd5wwMVkgK8qK_1.117.F13.imprint","IMPRINT",EDGE,{"derivedFrom":sQuery(id+"Fhpd5wwMVkgK8qK_1.117.F13.wireOp",EDGE,"E6")}),1.0]])]});
            var Q112;
            Q112=makeQuery(id+"Fhpd5wwMVkgK8qK_1.121.F13.imprint","IMPRINT",FACE,{"disambiguationData":[TD([[makeQuery(id+"Fhpd5wwMVkgK8qK_1.121.F13.imprint","IMPRINT",EDGE,{"derivedFrom":sQuery(id+"Fhpd5wwMVkgK8qK_1.121.F13.wireOp",EDGE,"E6")}),1.0]])]});
            var Q113;
            Q113=makeQuery(id+"Fhpd5wwMVkgK8qK_1.112.F13.imprint","IMPRINT",FACE,{"disambiguationData":[TD([[makeQuery(id+"Fhpd5wwMVkgK8qK_1.112.F13.imprint","IMPRINT",EDGE,{"derivedFrom":sQuery(id+"Fhpd5wwMVkgK8qK_1.112.F13.wireOp",EDGE,"E6")}),1.0]])]});
            var Q114;
            Q114=makeQuery(id+"Fhpd5wwMVkgK8qK_1.113.F13.imprint","IMPRINT",FACE,{"disambiguationData":[TD([[makeQuery(id+"Fhpd5wwMVkgK8qK_1.113.F13.imprint","IMPRINT",EDGE,{"derivedFrom":sQuery(id+"Fhpd5wwMVkgK8qK_1.113.F13.wireOp",EDGE,"E6")}),1.0]])]});
            var Q115;
            Q115=makeQuery(id+"Fhpd5wwMVkgK8qK_1.129.F13.imprint","IMPRINT",FACE,{"disambiguationData":[TD([[makeQuery(id+"Fhpd5wwMVkgK8qK_1.129.F13.imprint","IMPRINT",EDGE,{"derivedFrom":sQuery(id+"Fhpd5wwMVkgK8qK_1.129.F13.wireOp",EDGE,"E6")}),1.0]])]});
            var Q116;
            Q116=makeQuery(id+"Fhpd5wwMVkgK8qK_1.141.F13.imprint","IMPRINT",FACE,{"disambiguationData":[TD([[makeQuery(id+"Fhpd5wwMVkgK8qK_1.141.F13.imprint","IMPRINT",EDGE,{"derivedFrom":sQuery(id+"Fhpd5wwMVkgK8qK_1.141.F13.wireOp",EDGE,"E6")}),1.0]])]});
            var Q117;
            Q117=makeQuery(id+"Fhpd5wwMVkgK8qK_1.127.F13.imprint","IMPRINT",FACE,{"disambiguationData":[TD([[makeQuery(id+"Fhpd5wwMVkgK8qK_1.127.F13.imprint","IMPRINT",EDGE,{"derivedFrom":sQuery(id+"Fhpd5wwMVkgK8qK_1.127.F13.wireOp",EDGE,"E6")}),1.0]])]});
            var Q118;
            Q118=makeQuery(id+"Fhpd5wwMVkgK8qK_1.146.F13.imprint","IMPRINT",FACE,{"disambiguationData":[TD([[makeQuery(id+"Fhpd5wwMVkgK8qK_1.146.F13.imprint","IMPRINT",EDGE,{"derivedFrom":sQuery(id+"Fhpd5wwMVkgK8qK_1.146.F13.wireOp",EDGE,"E6")}),1.0]])]});
            var Q119;
            Q119=makeQuery(id+"Fhpd5wwMVkgK8qK_1.137.F13.imprint","IMPRINT",FACE,{"disambiguationData":[TD([[makeQuery(id+"Fhpd5wwMVkgK8qK_1.137.F13.imprint","IMPRINT",EDGE,{"derivedFrom":sQuery(id+"Fhpd5wwMVkgK8qK_1.137.F13.wireOp",EDGE,"E6")}),1.0]])]});
            var Q120;
            Q120=makeQuery(id+"Fhpd5wwMVkgK8qK_1.123.F13.imprint","IMPRINT",FACE,{"disambiguationData":[TD([[makeQuery(id+"Fhpd5wwMVkgK8qK_1.123.F13.imprint","IMPRINT",EDGE,{"derivedFrom":sQuery(id+"Fhpd5wwMVkgK8qK_1.123.F13.wireOp",EDGE,"E6")}),1.0]])]});
            var Q121;
            Q121=makeQuery(id+"Fhpd5wwMVkgK8qK_1.139.F13.imprint","IMPRINT",FACE,{"disambiguationData":[TD([[makeQuery(id+"Fhpd5wwMVkgK8qK_1.139.F13.imprint","IMPRINT",EDGE,{"derivedFrom":sQuery(id+"Fhpd5wwMVkgK8qK_1.139.F13.wireOp",EDGE,"E6")}),1.0]])]});
            var Q122;
            Q122=makeQuery(id+"Fhpd5wwMVkgK8qK_1.130.F13.imprint","IMPRINT",FACE,{"disambiguationData":[TD([[makeQuery(id+"Fhpd5wwMVkgK8qK_1.130.F13.imprint","IMPRINT",EDGE,{"derivedFrom":sQuery(id+"Fhpd5wwMVkgK8qK_1.130.F13.wireOp",EDGE,"E6")}),1.0]])]});
            var Q123;
            Q123=makeQuery(id+"Fhpd5wwMVkgK8qK_1.131.F13.imprint","IMPRINT",FACE,{"disambiguationData":[TD([[makeQuery(id+"Fhpd5wwMVkgK8qK_1.131.F13.imprint","IMPRINT",EDGE,{"derivedFrom":sQuery(id+"Fhpd5wwMVkgK8qK_1.131.F13.wireOp",EDGE,"E6")}),1.0]])]});
            var Q124;
            Q124=makeQuery(id+"Fhpd5wwMVkgK8qK_1.120.F13.imprint","IMPRINT",FACE,{"disambiguationData":[TD([[makeQuery(id+"Fhpd5wwMVkgK8qK_1.120.F13.imprint","IMPRINT",EDGE,{"derivedFrom":sQuery(id+"Fhpd5wwMVkgK8qK_1.120.F13.wireOp",EDGE,"E6")}),1.0]])]});
            var Q125;
            Q125=makeQuery(id+"Fhpd5wwMVkgK8qK_1.135.F13.imprint","IMPRINT",FACE,{"disambiguationData":[TD([[makeQuery(id+"Fhpd5wwMVkgK8qK_1.135.F13.imprint","IMPRINT",EDGE,{"derivedFrom":sQuery(id+"Fhpd5wwMVkgK8qK_1.135.F13.wireOp",EDGE,"E6")}),1.0]])]});
            var Q126;
            Q126=makeQuery(id+"Fhpd5wwMVkgK8qK_1.119.F13.imprint","IMPRINT",FACE,{"disambiguationData":[TD([[makeQuery(id+"Fhpd5wwMVkgK8qK_1.119.F13.imprint","IMPRINT",EDGE,{"derivedFrom":sQuery(id+"Fhpd5wwMVkgK8qK_1.119.F13.wireOp",EDGE,"E6")}),1.0]])]});
            var Q127;
            Q127=makeQuery(id+"Fhpd5wwMVkgK8qK_1.133.F13.imprint","IMPRINT",FACE,{"disambiguationData":[TD([[makeQuery(id+"Fhpd5wwMVkgK8qK_1.133.F13.imprint","IMPRINT",EDGE,{"derivedFrom":sQuery(id+"Fhpd5wwMVkgK8qK_1.133.F13.wireOp",EDGE,"E6")}),1.0]])]});
            var Q128;
            Q128=makeQuery(id+"Fhpd5wwMVkgK8qK_1.148.F13.imprint","IMPRINT",FACE,{"disambiguationData":[TD([[makeQuery(id+"Fhpd5wwMVkgK8qK_1.148.F13.imprint","IMPRINT",EDGE,{"derivedFrom":sQuery(id+"Fhpd5wwMVkgK8qK_1.148.F13.wireOp",EDGE,"E6")}),1.0]])]});
            var Q129;
            Q129=makeQuery(id+"Fhpd5wwMVkgK8qK_1.116.F13.imprint","IMPRINT",FACE,{"disambiguationData":[TD([[makeQuery(id+"Fhpd5wwMVkgK8qK_1.116.F13.imprint","IMPRINT",EDGE,{"derivedFrom":sQuery(id+"Fhpd5wwMVkgK8qK_1.116.F13.wireOp",EDGE,"E6")}),1.0]])]});
            var Q130;
            Q130=makeQuery(id+"Fhpd5wwMVkgK8qK_1.110.F13.imprint","IMPRINT",FACE,{"disambiguationData":[TD([[makeQuery(id+"Fhpd5wwMVkgK8qK_1.110.F13.imprint","IMPRINT",EDGE,{"derivedFrom":sQuery(id+"Fhpd5wwMVkgK8qK_1.110.F13.wireOp",EDGE,"E6")}),1.0]])]});
            var Q131;
            Q131=makeQuery(id+"Fhpd5wwMVkgK8qK_1.124.F13.imprint","IMPRINT",FACE,{"disambiguationData":[TD([[makeQuery(id+"Fhpd5wwMVkgK8qK_1.124.F13.imprint","IMPRINT",EDGE,{"derivedFrom":sQuery(id+"Fhpd5wwMVkgK8qK_1.124.F13.wireOp",EDGE,"E6")}),1.0]])]});
            var Q132;
            Q132=makeQuery(id+"Fhpd5wwMVkgK8qK_1.118.F13.imprint","IMPRINT",FACE,{"disambiguationData":[TD([[makeQuery(id+"Fhpd5wwMVkgK8qK_1.118.F13.imprint","IMPRINT",EDGE,{"derivedFrom":sQuery(id+"Fhpd5wwMVkgK8qK_1.118.F13.wireOp",EDGE,"E6")}),1.0]])]});
            var Q133;
            Q133=makeQuery(id+"Fhpd5wwMVkgK8qK_1.140.F13.imprint","IMPRINT",FACE,{"disambiguationData":[TD([[makeQuery(id+"Fhpd5wwMVkgK8qK_1.140.F13.imprint","IMPRINT",EDGE,{"derivedFrom":sQuery(id+"Fhpd5wwMVkgK8qK_1.140.F13.wireOp",EDGE,"E6")}),1.0]])]});
            var Q134;
            Q134=makeQuery(id+"Fhpd5wwMVkgK8qK_1.145.F13.imprint","IMPRINT",FACE,{"disambiguationData":[TD([[makeQuery(id+"Fhpd5wwMVkgK8qK_1.145.F13.imprint","IMPRINT",EDGE,{"derivedFrom":sQuery(id+"Fhpd5wwMVkgK8qK_1.145.F13.wireOp",EDGE,"E6")}),1.0]])]});
            var Q135;
            Q135=makeQuery(id+"Fhpd5wwMVkgK8qK_1.134.F13.imprint","IMPRINT",FACE,{"disambiguationData":[TD([[makeQuery(id+"Fhpd5wwMVkgK8qK_1.134.F13.imprint","IMPRINT",EDGE,{"derivedFrom":sQuery(id+"Fhpd5wwMVkgK8qK_1.134.F13.wireOp",EDGE,"E6")}),1.0]])]});
            var Q136;
            Q136=makeQuery(id+"Fhpd5wwMVkgK8qK_1.132.F13.imprint","IMPRINT",FACE,{"disambiguationData":[TD([[makeQuery(id+"Fhpd5wwMVkgK8qK_1.132.F13.imprint","IMPRINT",EDGE,{"derivedFrom":sQuery(id+"Fhpd5wwMVkgK8qK_1.132.F13.wireOp",EDGE,"E6")}),1.0]])]});
            var Q137;
            Q137=makeQuery(id+"Fhpd5wwMVkgK8qK_1.142.F13.imprint","IMPRINT",FACE,{"disambiguationData":[TD([[makeQuery(id+"Fhpd5wwMVkgK8qK_1.142.F13.imprint","IMPRINT",EDGE,{"derivedFrom":sQuery(id+"Fhpd5wwMVkgK8qK_1.142.F13.wireOp",EDGE,"E6")}),1.0]])]});
            var Q138;
            Q138=makeQuery(id+"Fhpd5wwMVkgK8qK_1.125.F13.imprint","IMPRINT",FACE,{"disambiguationData":[TD([[makeQuery(id+"Fhpd5wwMVkgK8qK_1.125.F13.imprint","IMPRINT",EDGE,{"derivedFrom":sQuery(id+"Fhpd5wwMVkgK8qK_1.125.F13.wireOp",EDGE,"E6")}),1.0]])]});
            var Q139;
            Q139=makeQuery(id+"Fhpd5wwMVkgK8qK_1.144.F13.imprint","IMPRINT",FACE,{"disambiguationData":[TD([[makeQuery(id+"Fhpd5wwMVkgK8qK_1.144.F13.imprint","IMPRINT",EDGE,{"derivedFrom":sQuery(id+"Fhpd5wwMVkgK8qK_1.144.F13.wireOp",EDGE,"E6")}),1.0]])]});
            var Q140;
            Q140=makeQuery(id+"Fhpd5wwMVkgK8qK_1.128.F13.imprint","IMPRINT",FACE,{"disambiguationData":[TD([[makeQuery(id+"Fhpd5wwMVkgK8qK_1.128.F13.imprint","IMPRINT",EDGE,{"derivedFrom":sQuery(id+"Fhpd5wwMVkgK8qK_1.128.F13.wireOp",EDGE,"E6")}),1.0]])]});
            var Q141;
            Q141=makeQuery(id+"Fhpd5wwMVkgK8qK_1.126.F13.imprint","IMPRINT",FACE,{"disambiguationData":[TD([[makeQuery(id+"Fhpd5wwMVkgK8qK_1.126.F13.imprint","IMPRINT",EDGE,{"derivedFrom":sQuery(id+"Fhpd5wwMVkgK8qK_1.126.F13.wireOp",EDGE,"E6")}),1.0]])]});
            var Q142;
            Q142=makeQuery(id+"Fhpd5wwMVkgK8qK_1.114.F13.imprint","IMPRINT",FACE,{"disambiguationData":[TD([[makeQuery(id+"Fhpd5wwMVkgK8qK_1.114.F13.imprint","IMPRINT",EDGE,{"derivedFrom":sQuery(id+"Fhpd5wwMVkgK8qK_1.114.F13.wireOp",EDGE,"E6")}),1.0]])]});
            var Q143;
            Q143=makeQuery(id+"Fhpd5wwMVkgK8qK_1.111.F13.imprint","IMPRINT",FACE,{"disambiguationData":[TD([[makeQuery(id+"Fhpd5wwMVkgK8qK_1.111.F13.imprint","IMPRINT",EDGE,{"derivedFrom":sQuery(id+"Fhpd5wwMVkgK8qK_1.111.F13.wireOp",EDGE,"E6")}),1.0]])]});
            var Q144;
            Q144=makeQuery(id+"Fhpd5wwMVkgK8qK_1.149.F13.imprint","IMPRINT",FACE,{"disambiguationData":[TD([[makeQuery(id+"Fhpd5wwMVkgK8qK_1.149.F13.imprint","IMPRINT",EDGE,{"derivedFrom":sQuery(id+"Fhpd5wwMVkgK8qK_1.149.F13.wireOp",EDGE,"E6")}),1.0]])]});
            var Q145;
            Q145=makeQuery(id+"Fhpd5wwMVkgK8qK_1.143.F13.imprint","IMPRINT",FACE,{"disambiguationData":[TD([[makeQuery(id+"Fhpd5wwMVkgK8qK_1.143.F13.imprint","IMPRINT",EDGE,{"derivedFrom":sQuery(id+"Fhpd5wwMVkgK8qK_1.143.F13.wireOp",EDGE,"E6")}),1.0]])]});
            var Q146;
            Q146=makeQuery(id+"Fhpd5wwMVkgK8qK_1.115.F13.imprint","IMPRINT",FACE,{"disambiguationData":[TD([[makeQuery(id+"Fhpd5wwMVkgK8qK_1.115.F13.imprint","IMPRINT",EDGE,{"derivedFrom":sQuery(id+"Fhpd5wwMVkgK8qK_1.115.F13.wireOp",EDGE,"E6")}),1.0]])]});
            var Q147;
            Q147=makeQuery(id+"Fhpd5wwMVkgK8qK_1.136.F13.imprint","IMPRINT",FACE,{"disambiguationData":[TD([[makeQuery(id+"Fhpd5wwMVkgK8qK_1.136.F13.imprint","IMPRINT",EDGE,{"derivedFrom":sQuery(id+"Fhpd5wwMVkgK8qK_1.136.F13.wireOp",EDGE,"E6")}),1.0]])]});
            var Q148;
            Q148=makeQuery(id+"Fhpd5wwMVkgK8qK_1.122.F13.imprint","IMPRINT",FACE,{"disambiguationData":[TD([[makeQuery(id+"Fhpd5wwMVkgK8qK_1.122.F13.imprint","IMPRINT",EDGE,{"derivedFrom":sQuery(id+"Fhpd5wwMVkgK8qK_1.122.F13.wireOp",EDGE,"E6")}),1.0]])]});
            var Q149;
            Q149=makeQuery(id+"Fhpd5wwMVkgK8qK_1.138.F13.imprint","IMPRINT",FACE,{"disambiguationData":[TD([[makeQuery(id+"Fhpd5wwMVkgK8qK_1.138.F13.imprint","IMPRINT",EDGE,{"derivedFrom":sQuery(id+"Fhpd5wwMVkgK8qK_1.138.F13.wireOp",EDGE,"E6")}),1.0]])]});
            extrude(context, id + "F16", {"entities" : qUnion([Q0, Q1, Q2, Q3, Q4, Q5, Q6, Q7, Q8, Q9, Q10, Q11, Q12, Q13, Q14, Q15, Q16, Q17, Q18, Q19, Q20, Q21, Q22, Q23, Q24, Q25, Q26, Q27, Q28, Q29, Q30, Q31, Q32, Q33, Q34, Q35, Q36, Q37, Q38, Q39, Q40, Q41, Q42, Q43, Q44, Q45, Q46, Q47, Q48, Q49, Q50, Q51, Q52, Q53, Q54, Q55, Q56, Q57, Q58, Q59, Q60, Q61, Q62, Q63, Q64, Q65, Q66, Q67, Q68, Q69, Q70, Q71, Q72, Q73, Q74, Q75, Q76, Q77, Q78, Q79, Q80, Q81, Q82, Q83, Q84, Q85, Q86, Q87, Q88, Q89, Q90, Q91, Q92, Q93, Q94, Q95, Q96, Q97, Q98, Q99, Q100, Q101, Q102, Q103, Q104, Q105, Q106, Q107, Q108, Q109, Q110, Q111, Q112, Q113, Q114, Q115, Q116, Q117, Q118, Q119, Q120, Q121, Q122, Q123, Q124, Q125, Q126, Q127, Q128, Q129, Q130, Q131, Q132, Q133, Q134, Q135, Q136, Q137, Q138, Q139, Q140, Q141, Q142, Q143, Q144, Q145, Q146, Q147, Q148, Q149]), "operationType" : NewBodyOperationType.REMOVE, "oppositeDirection" : true, "depth" : 20.32 * mm, "offsetDistance" : 25.4 * mm});
        }
    });
